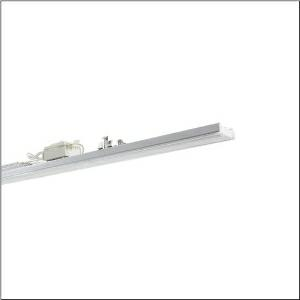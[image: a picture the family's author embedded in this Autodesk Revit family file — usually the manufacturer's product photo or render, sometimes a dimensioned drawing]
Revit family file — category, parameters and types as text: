
# Revit family: licross_21_recessed_ho_52tl18dn4e5m
name_source: partatom
category: Lighting Fixtures
units: mm (PartAtom-declared; Revit-internal decimal feet)

## family parameters
Cut with Voids When Loaded = No
Host = Face
Light Source = No
Part Type = Normal
Room Calculation Point = No
Round Connector Dimension = Use Diameter
Shared = No

## types (1)
- --- (1 x LED, 14850 lm, 84.6 W, 4000K)
    Apparent Load = 85 VA
    CIE Flux Codes = 75 94 99 100 100
    Color Rendering = 80
    Color Temperature = 4000K
    Default Elevation = 1800 mm
    Description = Licross 21 Recessed HO, luminaire insert, of sheet steel, galvanised, coil coated, white, length: 1.500mm, width: 66mm, height: 67mm, LED rated luminous flux: 14.850lm, light colour: 840, SDCM (Standard Deviation of Colour Matching)MacAdam ≤ 3 SDCM (initial), control gear: DALI 2, with plug, 5-pole, with phase selection, mains connection: 220..240V, AC, 50/60Hz, rated input power: 85W, internal wiring halogen-free, primary light control with lens, of plastic, primary optical cover: cover, of PMMA, light emission: direct distribution, primary light characteristic: symmetric, protection rating (complete): IP40, insulation class (complete): insulation class I (protective earthing), certification: CE, ENEC, VDE, UKCA, protection symbol: D if used in an environment without relevant dust loads with corresponding accessories, impact resistance: IK06, permissible ambient temperature for indoor applications: -25..+30°C, corresponds to IFS (International Featured Standards) requirements for safety and quality in the food industry, reducing of maximum allowable ambient temperature of 5°C with ceiling mounting, LABS conformity tested according to VDMA 24364:2018-05, The light source and the operating device comply with the requirements of the Ecodesign Regulation (EU) 2019/2020 and are replaceable in accordance with this regulation, packaging unit: 1 piece
    Height = 58 mm
    Lamp = 1 x LED
    Lamp Light Flux = 14850 lm
    Lamp Power = 84.6 W
    Lamp count = 1
    Length = 1500 mm
    Luminous efficacy = 176 lm/W
    Manufacturer = Siteco
    ModVariant = No
    Model = 52TL18DN4E5M
    Mounting Place = Ceiling
    Mounting Type = Pendant
    Number of Poles = 1
    OnlyDefault = Yes
    Power Factor = 1
    Product Name = Licross 21 Recessed HO
    Product group = luminaire insert | ceiling pendant
    ProductGroupID = 901
    Protection Class = Protection class I
    Protection Degree = IP 40
    RLX_Detail_Level = 1
    RLX_Emergency_Light_Flux = 0 lm
    RLX_Emergency_Type = 0
    RLX_Emergency_Type_DB = No
    RlxData = <blob elided: 24969 chars, md5=2e5c4bbd>
    Socket = socket
    Standby Power = 0 W
    System Light Flux = 14850 lm
    System Power = 85 W
    Type Comments = factory setting: luminous flux: 100 % | dim-lin: 254 | 484 mA
    Type Image = l_1296930.jpg
    URL = http://relux.com
    VarID = @adj_125919
    Voltage = 0 V
    Weight = 0.00 kg
    Width = 66 mm

## geometry (parser evidence)
native form markers: Blend x4, Sweep x11
no freeform markers — native parametric forms only
